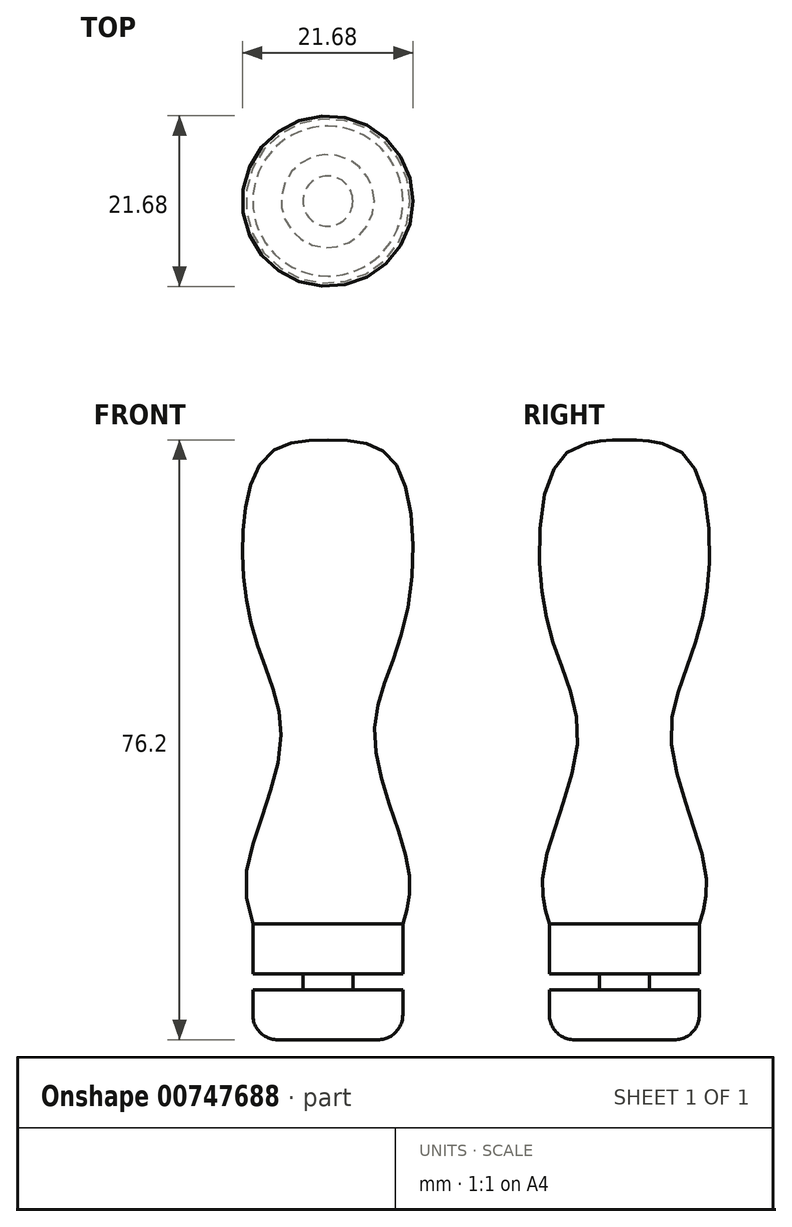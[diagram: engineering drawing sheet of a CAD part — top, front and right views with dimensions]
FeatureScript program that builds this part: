
annotation { "Feature Type Name" : "Feature", "Feature Type Description" : "" }
export const myFeature = defineFeature(function(context is Context, id is Id, definition is map)
    precondition{}
    {
        {
            var Q0;
            Q0=qCreatedBy(makeId("Front.planeOp"),FACE);
            var sketch = newSketch(context, id + "F0", { "sketchPlane" : qUnion([Q0])});
            skLineSegment(sketch, "E0", {"start": v(0, 0) * mm, "end": v(0, 76.2) * mm});
            skLineSegment(sketch, "E1", {"start": v(0, 0) * mm, "end": v(6.35, 0) * mm});
            skLineSegment(sketch, "E2", {"start": v(9.53, 3.18) * mm, "end": v(9.53, 6.35) * mm});
            skLineSegment(sketch, "E3", {"start": v(9.53, 6.35) * mm, "end": v(3.18, 6.35) * mm});
            skPoint(sketch, "E4.visualSharp", {"position": v(9.53, 0) * mm});
            skArc(sketch, "E4.filletArc", {"start": v(6.35, 0) * mm, "mid": v(8.6, 0.93) * mm, "end": v(9.53, 3.18) * mm});
            skLineSegment(sketch, "E5", {"start": v(3.18, 6.35) * mm, "end": v(3.18, 8.35) * mm});
            skLineSegment(sketch, "E6", {"start": v(3.17, 8.35) * mm, "end": v(9.52, 8.35) * mm});
            skLineSegment(sketch, "E7", {"start": v(9.53, 8.35) * mm, "end": v(9.53, 14.7) * mm});
            skFitSpline(sketch, "E8", {"points": [v(0, 76.2) * mm, v(8.3, 73.57) * mm, v(9.84, 53.29) * mm, v(5.92, 38.47) * mm, v(10.26, 21.69) * mm, v(9.53, 14.7) * mm], "startDerivative": vector(58.62, -1.04) * mm, "endDerivative": vector(-12.46, -41.81) * mm});
            skSolve(sketch);
        }
        {
            var Q0;
            Q0=makeQuery(id+"F0.imprint","IMPRINT",FACE,{"disambiguationData":[TD([[makeQuery(id+"F0.imprint","IMPRINT",EDGE,{"derivedFrom":sQuery(id+"F0.wireOp",EDGE,"E0")}),-1.0]])]});
            var Q1;
            Q1=sQuery(id+"F0.wireOp",EDGE,"E0");
            revolve(context, id + "F1", {"surfaceOperationType" : NewSurfaceOperationType.NEW, "entities" : qUnion([Q0]), "axis" : qUnion([Q1]), "revolveType" : RevolveType.FULL});
        }
    });
